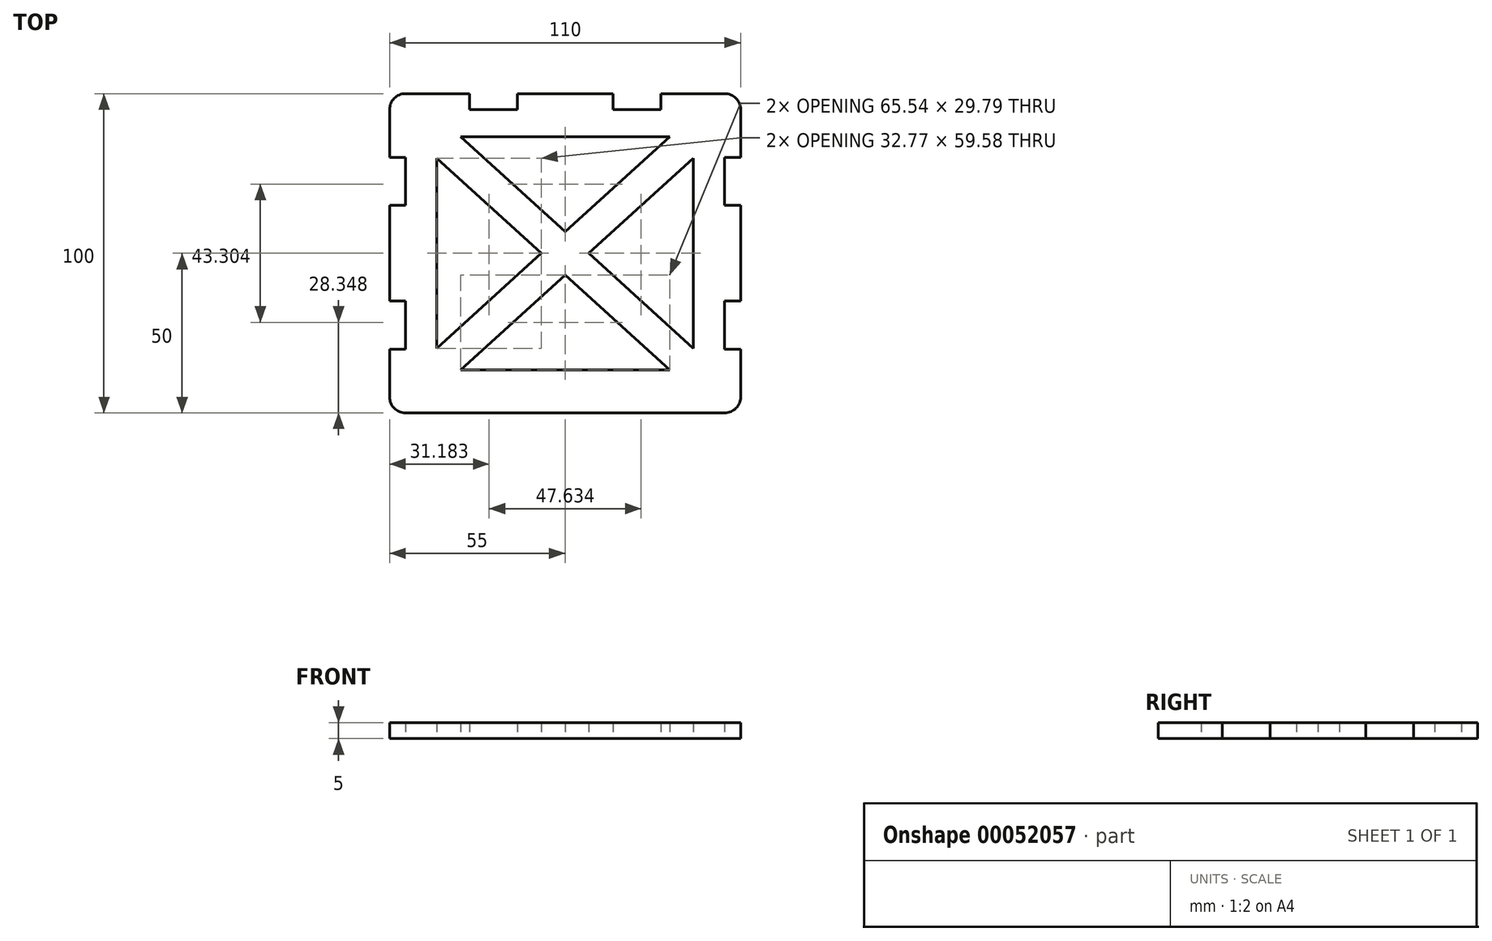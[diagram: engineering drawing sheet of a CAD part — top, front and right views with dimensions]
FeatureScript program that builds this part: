
annotation { "Feature Type Name" : "Feature", "Feature Type Description" : "" }
export const myFeature = defineFeature(function(context is Context, id is Id, definition is map)
    precondition{}
    {
        {
            var Q0;
            Q0=qCreatedBy(makeId("Top.planeOp"),FACE);
            var sketch = newSketch(context, id + "F0", { "sketchPlane" : qUnion([Q0])});
            skLineSegment(sketch, "E0.top", {"start": v(-55, -50) * mm, "end": v(55, -50) * mm});
            skLineSegment(sketch, "E0.left", {"start": v(-55, 50) * mm, "end": v(-55, 30) * mm});
            skLineSegment(sketch, "E0.right", {"start": v(55, 50) * mm, "end": v(55, 30) * mm});
            skLineSegment(sketch, "E1", {"start": v(-55, -30) * mm, "end": v(-50, -30) * mm});
            skLineSegment(sketch, "E2", {"start": v(-50, -30) * mm, "end": v(-50, -15) * mm});
            skLineSegment(sketch, "E3", {"start": v(-50, -15) * mm, "end": v(-55, -15) * mm});
            skLineSegment(sketch, "E4", {"start": v(-55, 30) * mm, "end": v(-50, 30) * mm});
            skLineSegment(sketch, "E5", {"start": v(-50, 30) * mm, "end": v(-50, 15) * mm});
            skLineSegment(sketch, "E6", {"start": v(-50, 15) * mm, "end": v(-55, 15) * mm});
            skLineSegment(sketch, "E7", {"start": v(55, 30) * mm, "end": v(50, 30) * mm});
            skLineSegment(sketch, "E8", {"start": v(50, 30) * mm, "end": v(50, 15) * mm});
            skLineSegment(sketch, "E9", {"start": v(50, 15) * mm, "end": v(55, 15) * mm});
            skLineSegment(sketch, "E10", {"start": v(55, -15) * mm, "end": v(50, -15) * mm});
            skLineSegment(sketch, "E11", {"start": v(50, -15) * mm, "end": v(50, -30) * mm});
            skLineSegment(sketch, "E12", {"start": v(50, -30) * mm, "end": v(55, -30) * mm});
            skLineSegment(sketch, "E13.trimOffspring", {"start": v(55, 15) * mm, "end": v(55, -15) * mm});
            skLineSegment(sketch, "E14.trimOffspring", {"start": v(55, -30) * mm, "end": v(55, -50) * mm});
            skLineSegment(sketch, "E15.trimOffspring", {"start": v(-55, -30) * mm, "end": v(-55, -50) * mm});
            skLineSegment(sketch, "E16.trimOffspring", {"start": v(-55, 15) * mm, "end": v(-55, -15) * mm});
            skLineSegment(sketch, "E17", {"start": v(-55, 50) * mm, "end": v(-30, 50) * mm});
            skLineSegment(sketch, "E18", {"start": v(-30, 50) * mm, "end": v(-30, 45) * mm});
            skLineSegment(sketch, "E19", {"start": v(-30, 45) * mm, "end": v(-15, 45) * mm});
            skLineSegment(sketch, "E20", {"start": v(-15, 45) * mm, "end": v(-15, 50) * mm});
            skLineSegment(sketch, "E21", {"start": v(-15, 50) * mm, "end": v(15, 50) * mm});
            skLineSegment(sketch, "E22", {"start": v(15, 50) * mm, "end": v(15, 45) * mm});
            skLineSegment(sketch, "E23", {"start": v(15, 45) * mm, "end": v(30, 45) * mm});
            skLineSegment(sketch, "E24", {"start": v(30, 45) * mm, "end": v(30, 50) * mm});
            skLineSegment(sketch, "E25", {"start": v(30, 50) * mm, "end": v(55, 50) * mm});
            skLineSegment(sketch, "E26", {"start": v(0, 50) * mm, "end": v(0, -50) * mm, "construction": true});
            skLineSegment(sketch, "E27.rect.bottom", {"start": v(32.77, 36.55) * mm, "end": v(-32.77, 36.55) * mm});
            skLineSegment(sketch, "E27.rect.top", {"start": v(32.77, -36.55) * mm, "end": v(-32.77, -36.55) * mm});
            skLineSegment(sketch, "E27.rect.left", {"start": v(40.2, 29.79) * mm, "end": v(40.2, -29.79) * mm});
            skLineSegment(sketch, "E27.rect.right", {"start": v(-40.2, 29.79) * mm, "end": v(-40.2, -29.79) * mm});
            skPoint(sketch, "E27.rect.middle", {"position": v(0, 0) * mm});
            skLineSegment(sketch, "E28", {"start": v(-32.77, -36.55) * mm, "end": v(0, -6.76) * mm});
            skLineSegment(sketch, "E29", {"start": v(32.77, 36.55) * mm, "end": v(0, 6.76) * mm});
            skLineSegment(sketch, "E30", {"start": v(32.77, -36.55) * mm, "end": v(0, -6.76) * mm});
            skLineSegment(sketch, "E31", {"start": v(-32.77, 36.55) * mm, "end": v(0, 6.76) * mm});
            skLineSegment(sketch, "E32.trimOffspring", {"start": v(7.43, 0) * mm, "end": v(40.2, -29.79) * mm});
            skLineSegment(sketch, "E33.trimOffspring", {"start": v(-7.43, 0) * mm, "end": v(-40.2, 29.79) * mm});
            skLineSegment(sketch, "E34.trimOffspring", {"start": v(7.43, 0) * mm, "end": v(40.2, 29.79) * mm});
            skLineSegment(sketch, "E35.trimOffspring", {"start": v(-7.43, 0) * mm, "end": v(-40.2, -29.79) * mm});
            skLineSegment(sketch, "E36", {"start": v(-55, 0) * mm, "end": v(55, 0) * mm, "construction": true});
            skSolve(sketch);
        }
        {
            var Q0;
            Q0=makeQuery(id+"F0.imprint","IMPRINT",FACE,{"disambiguationData":[TD([[makeQuery(id+"F0.imprint","IMPRINT",EDGE,{"derivedFrom":sQuery(id+"F0.wireOp",EDGE,"E0.top")}),1.0]])]});
            extrude(context, id + "F1", {"entities" : qUnion([Q0]), "depth" : 5 * mm});
        }
        {
            var Q0;
            Q0=makeQuery(id+"F1.opExtrude","SWEPT_EDGE",EDGE,{"disambiguationData":[OSD([sQuery(id+"F0.wireOp",EDGE,"E0.right"),sQuery(id+"F0.wireOp",EDGE,"E25")])]});
            var Q1;
            Q1=makeQuery(id+"F1.opExtrude","SWEPT_EDGE",EDGE,{"disambiguationData":[OSD([sQuery(id+"F0.wireOp",EDGE,"E0.left"),sQuery(id+"F0.wireOp",EDGE,"E17")])]});
            fillet(context, id + "F2", {"entities" : qUnion([Q0, Q1]), "radius" : 5 * mm, "tangentPropagation" : true, "allowEdgeOverflow" : false});
        }
        {
            var Q0;
            Q0=makeQuery(id+"F1.opExtrude","SWEPT_EDGE",EDGE,{"disambiguationData":[OSD([sQuery(id+"F0.wireOp",EDGE,"E0.top"),sQuery(id+"F0.wireOp",EDGE,"E14.trimOffspring")])]});
            var Q1;
            Q1=makeQuery(id+"F1.opExtrude","SWEPT_EDGE",EDGE,{"disambiguationData":[OSD([sQuery(id+"F0.wireOp",EDGE,"E0.top"),sQuery(id+"F0.wireOp",EDGE,"E15.trimOffspring")])]});
            fillet(context, id + "F3", {"entities" : qUnion([Q0, Q1]), "radius" : 5 * mm, "tangentPropagation" : true, "allowEdgeOverflow" : false});
        }
    });
